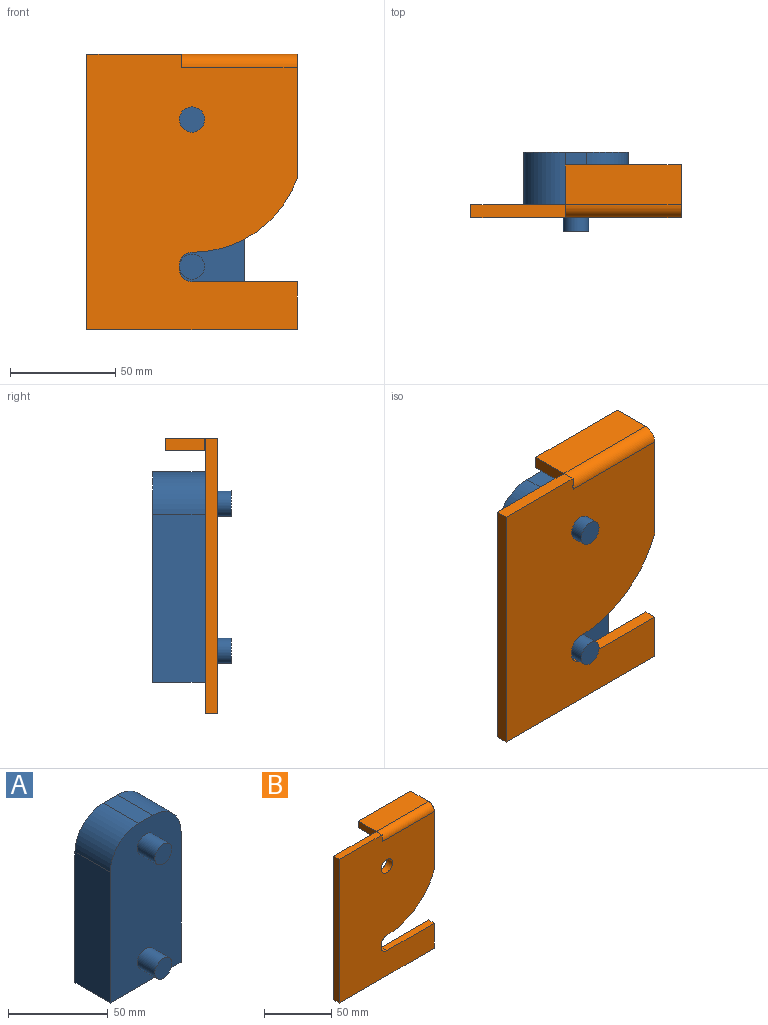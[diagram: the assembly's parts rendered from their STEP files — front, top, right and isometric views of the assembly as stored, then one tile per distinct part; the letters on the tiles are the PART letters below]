
ASSEMBLY  parts=2 mates=1
PART A: 16 faces, bbox 50x37.5x100 mm
  f0: cylinder r=6mm len=12.5mm, axis (0,-1,0), area 471.2mm2, adj f6,f13
  f1: cylinder r=6mm len=12.5mm, axis (0,-1,0), area 471.2mm2, adj f6,f10
  f2: plane 25x10mm, normal (0,0,1), area 250mm2, adj f6,f7,f14,f15
  f3: plane 80x25mm, normal (-1,0,0), area 2000mm2, adj f4,f6,f7,f14
  f4: plane 50x25mm, normal (0,0,-1), area 1250mm2, adj f3,f5,f6,f7
  f5: plane 80x25mm, normal (1,0,0), area 2000mm2, adj f4,f6,f7,f15
  f6: plane 100x50mm, normal (0,1,0), area 4602.1mm2, adj f0,f1,f2,f3,f4,f5,f14,f15
  f7: plane 100x50mm, normal (0,-1,0), area 4602.1mm2, adj f2,f3,f4,f5,f9,f12,f14,f15
  f8: plane 12x12mm, normal (0,-1,0), area 113.1mm2, adj f9
  f9: cylinder r=6mm len=12.5mm, axis (0,1,0), area 471.2mm2, adj f7,f8
  f10: plane 12x12mm, normal (0,1,0), area 113.1mm2, adj f1
  f11: plane 12x12mm, normal (0,-1,0), area 113.1mm2, adj f12
  f12: cylinder r=6mm len=12.5mm, axis (0,1,0), area 471.2mm2, adj f7,f11
  f13: plane 12x12mm, normal (0,1,0), area 113.1mm2, adj f0
  f14: cylinder r=20mm len=25mm, axis (0,1,0), area 785.4mm2, adj f2,f3,f6,f7
  f15: cylinder r=20mm len=25mm, axis (0,-1,0), area 785.4mm2, adj f2,f5,f6,f7
PART B: 23 faces, bbox 100x25x131 mm
  f0: plane 6.1x6mm, normal (1,0,0), area 8mm2, adj f2,f12,f13,f21
  f1: plane 53.07x6mm, normal (1,0,0), area 318.4mm2, adj f11,f12,f13,f20
  f2: plane 45x6mm, normal (0,0,1), area 270mm2, adj f0,f3,f12,f13
  f3: plane 131x6mm, normal (-1,0,0), area 786mm2, adj f2,f4,f12,f13
  f4: plane 100x6mm, normal (0,0,-1), area 600mm2, adj f3,f5,f12,f13
  f5: plane 22.8x6mm, normal (1,0,0), area 136.8mm2, adj f4,f6,f12,f13
  f6: plane 50x6mm, normal (0,0,1), area 300mm2, adj f5,f7,f12,f13
  f7: cylinder r=6mm len=6mm, axis (0,-1,0), area 56.5mm2, adj f6,f8,f12,f13
  f8: plane 6x2mm, normal (1,0,0), area 12mm2, adj f7,f9,f12,f13
  f9: cylinder r=6mm len=6mm, axis (0,-1,0), area 56.5mm2, adj f8,f11,f12,f13
  f10: cylinder r=6mm len=12mm, axis (0,-1,0), area 226.2mm2, adj f12,f13
  f11: cylinder r=53.2mm len=50mm, axis (0,-1,0), area 390.1mm2, adj f1,f9,f12,f13
  f12: plane 131x100mm, normal (0,-1,0), area 11406.7mm2, adj f0,f1,f2,f3,f4,f5,f6,f7
  f13: plane 131x100mm, normal (0,1,0), area 11406.7mm2, adj f0,f1,f2,f3,f4,f5,f6,f7
  f14: plane 6.1x0.1mm, normal (-1,0,0), area 0.6mm2, adj f13,f16,f21,f22
  f15: plane 55x6mm, normal (0,1,0), area 330mm2, adj f16,f17,f18,f19
  f16: plane 18.9x6mm, normal (-1,0,0), area 113.4mm2, adj f14,f15,f18,f19
  f17: plane 18.9x6mm, normal (1,0,0), area 113.4mm2, adj f15,f18,f19,f20
  f18: plane 55x18.9mm, normal (0,0,1), area 1039.5mm2, adj f15,f16,f17,f21
  f19: plane 55x18.9mm, normal (0,0,-1), area 1039.5mm2, adj f15,f16,f17,f22
  f20: plane 6.1x6.1mm, normal (1,0,0), area 29.2mm2, adj f1,f17,f21,f22
  f21: cylinder r=6.1mm len=55mm, axis (-1,0,0), area 527mm2, adj f0,f12,f14,f18,f20
  f22: cylinder r=0.1mm len=55mm, axis (-1,0,0), area 8.6mm2, adj f13,f14,f19,f20
PLACE A at identity
PLACE B t=(0,-6,0)mm fixed
MATE revolute A.f1 <-> B.f10  axis (0,-1,0) through (0,0,0)mm
